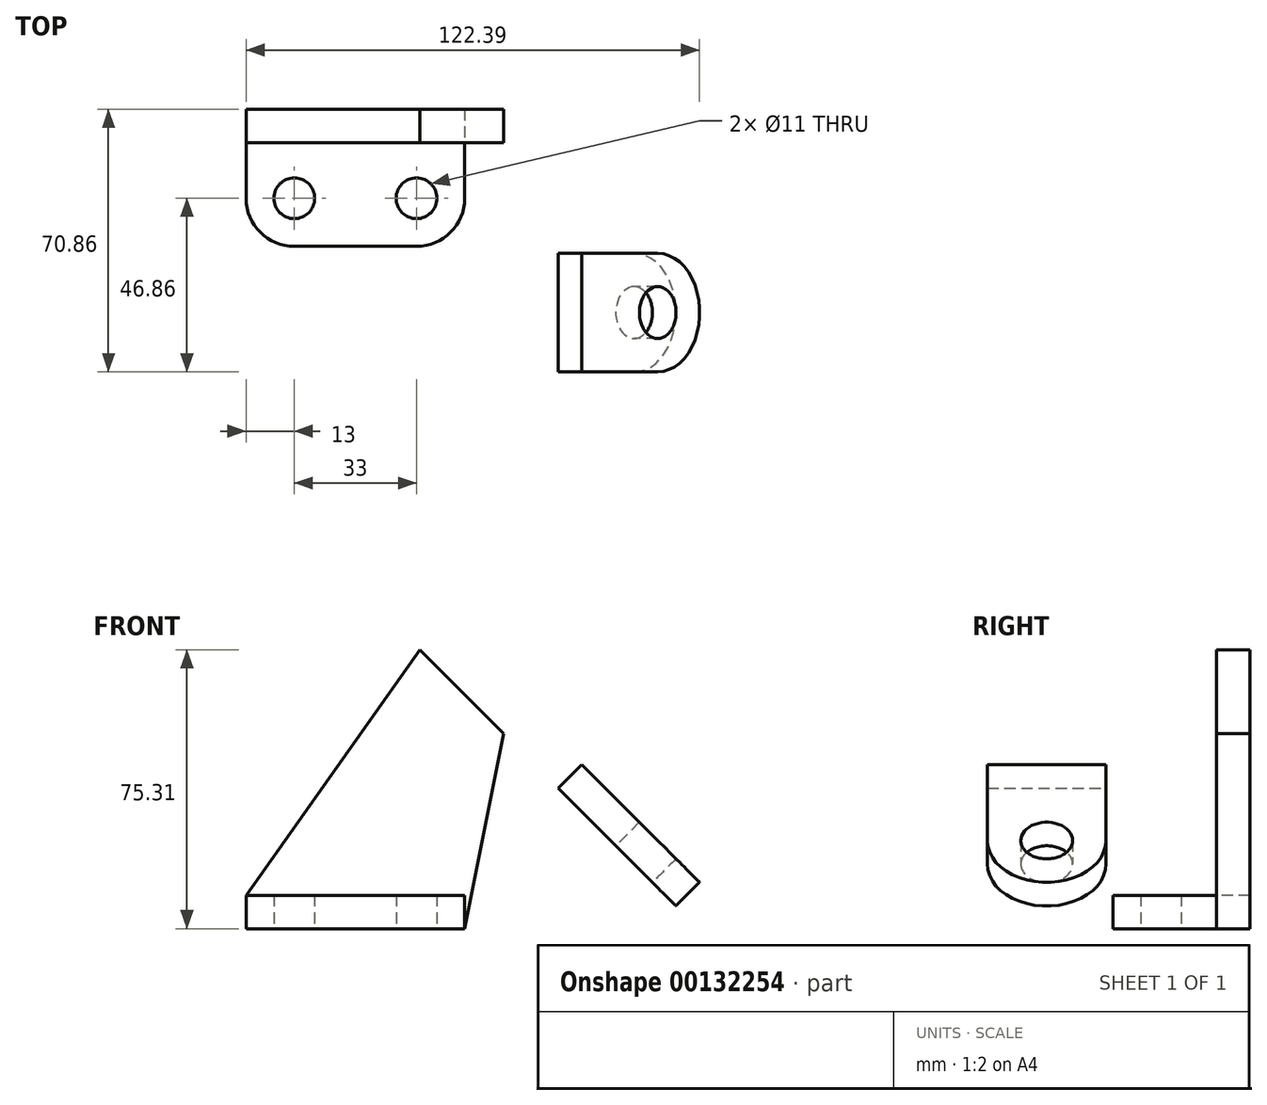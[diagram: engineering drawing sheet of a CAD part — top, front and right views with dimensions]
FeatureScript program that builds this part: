
annotation { "Feature Type Name" : "Feature", "Feature Type Description" : "" }
export const myFeature = defineFeature(function(context is Context, id is Id, definition is map)
    precondition{}
    {
        {
            var Q0;
            Q0=qCreatedBy(makeId("Top.planeOp"),FACE);
            var sketch = newSketch(context, id + "F0", { "sketchPlane" : qUnion([Q0])});
            skLineSegment(sketch, "E0.bottom", {"start": v(0, 0) * mm, "end": v(-59, 0) * mm});
            skLineSegment(sketch, "E0.top", {"start": v(-13, -28) * mm, "end": v(-46, -28) * mm});
            skLineSegment(sketch, "E0.left", {"start": v(0, 0) * mm, "end": v(0, -15) * mm});
            skLineSegment(sketch, "E0.right", {"start": v(-59, 0) * mm, "end": v(-59, -15) * mm});
            skPoint(sketch, "E1.visualSharp", {"position": v(-59, -28) * mm});
            skArc(sketch, "E1.filletArc", {"start": v(-59, -15) * mm, "mid": v(-55.2, -24.2) * mm, "end": v(-46, -28) * mm});
            skPoint(sketch, "E2.visualSharp", {"position": v(0, -28) * mm});
            skArc(sketch, "E2.filletArc", {"start": v(-13, -28) * mm, "mid": v(-3.8, -24.2) * mm, "end": v(0, -15) * mm});
            skCircle(sketch, "E3", {"center": v(-46, -15) * mm, "radius": 5.5 * mm});
            skCircle(sketch, "E4", {"center": v(-13, -15) * mm, "radius": 5.5 * mm});
            skSolve(sketch);
        }
        {
            var Q0;
            Q0=makeQuery(id+"F0.imprint","IMPRINT",FACE,{"disambiguationData":[TD([[makeQuery(id+"F0.imprint","IMPRINT",EDGE,{"derivedFrom":sQuery(id+"F0.wireOp",EDGE,"E0.bottom")}),1.0]])]});
            extrude(context, id + "F1", {"entities" : qUnion([Q0]), "depth" : 9 * mm});
        }
        {
            var Q0;
            Q0=makeQuery(id+"F1.opExtrude","SWEPT_FACE",FACE,{"disambiguationData":[OSD([sQuery(id+"F0.wireOp",EDGE,"E0.bottom")])]});
            var sketch = newSketch(context, id + "F2", { "sketchPlane" : qUnion([Q0])});
            skLineSegment(sketch, "E5", {"start": v(59, 9) * mm, "end": v(12.16, 75.31) * mm});
            skLineSegment(sketch, "E6", {"start": v(59, 9) * mm, "end": v(59, 0) * mm});
            skLineSegment(sketch, "E7", {"start": v(59, 0) * mm, "end": v(0, 0) * mm});
            skLineSegment(sketch, "E8", {"start": v(0, 0) * mm, "end": v(-10.46, 52.69) * mm});
            skLineSegment(sketch, "E9", {"start": v(-10.46, 52.69) * mm, "end": v(12.16, 75.31) * mm});
            skLineSegment(sketch, "E10", {"start": v(0.85, 64) * mm, "end": v(-40.67, 64) * mm, "construction": true});
            skSolve(sketch);
        }
        {
            var Q0;
            Q0 = qSketchRegion(id + "F2", true);
            extrude(context, id + "F3", {"entities" : qUnion([Q0]), "operationType" : NewBodyOperationType.ADD, "depth" : 9 * mm});
        }
        {
            var Q0;
            Q0=makeQuery(id+"F3.opExtrude","SWEPT_FACE",FACE,{"disambiguationData":[OSD([sQuery(id+"F2.wireOp",EDGE,"E9")])]});
            var sketch = newSketch(context, id + "F4", { "sketchPlane" : qUnion([Q0])});
            skLineSegment(sketch, "E11", {"start": v(-61.86, 9) * mm, "end": v(-61.86, -20) * mm});
            skPoint(sketch, "E11.endSnap0", {"position": v(-61.86, 4.5) * mm});
            skLineSegment(sketch, "E12", {"start": v(-61.86, 9) * mm, "end": v(-29.86, 9) * mm});
            skLineSegment(sketch, "E13", {"start": v(-29.86, 9) * mm, "end": v(-29.86, -20) * mm});
            skArc(sketch, "E14", {"start": v(-61.86, -20) * mm, "mid": v(-45.86, -36) * mm, "end": v(-29.86, -20) * mm});
            skCircle(sketch, "E15", {"center": v(-45.86, -20) * mm, "radius": 7 * mm});
            skSolve(sketch);
        }
        {
            var Q0;
            Q0 = qSketchRegion(id + "F4", true);
            extrude(context, id + "F5", {"entities" : qUnion([Q0]), "operationType" : NewBodyOperationType.ADD, "depth" : 9 * mm});
        }
    });
